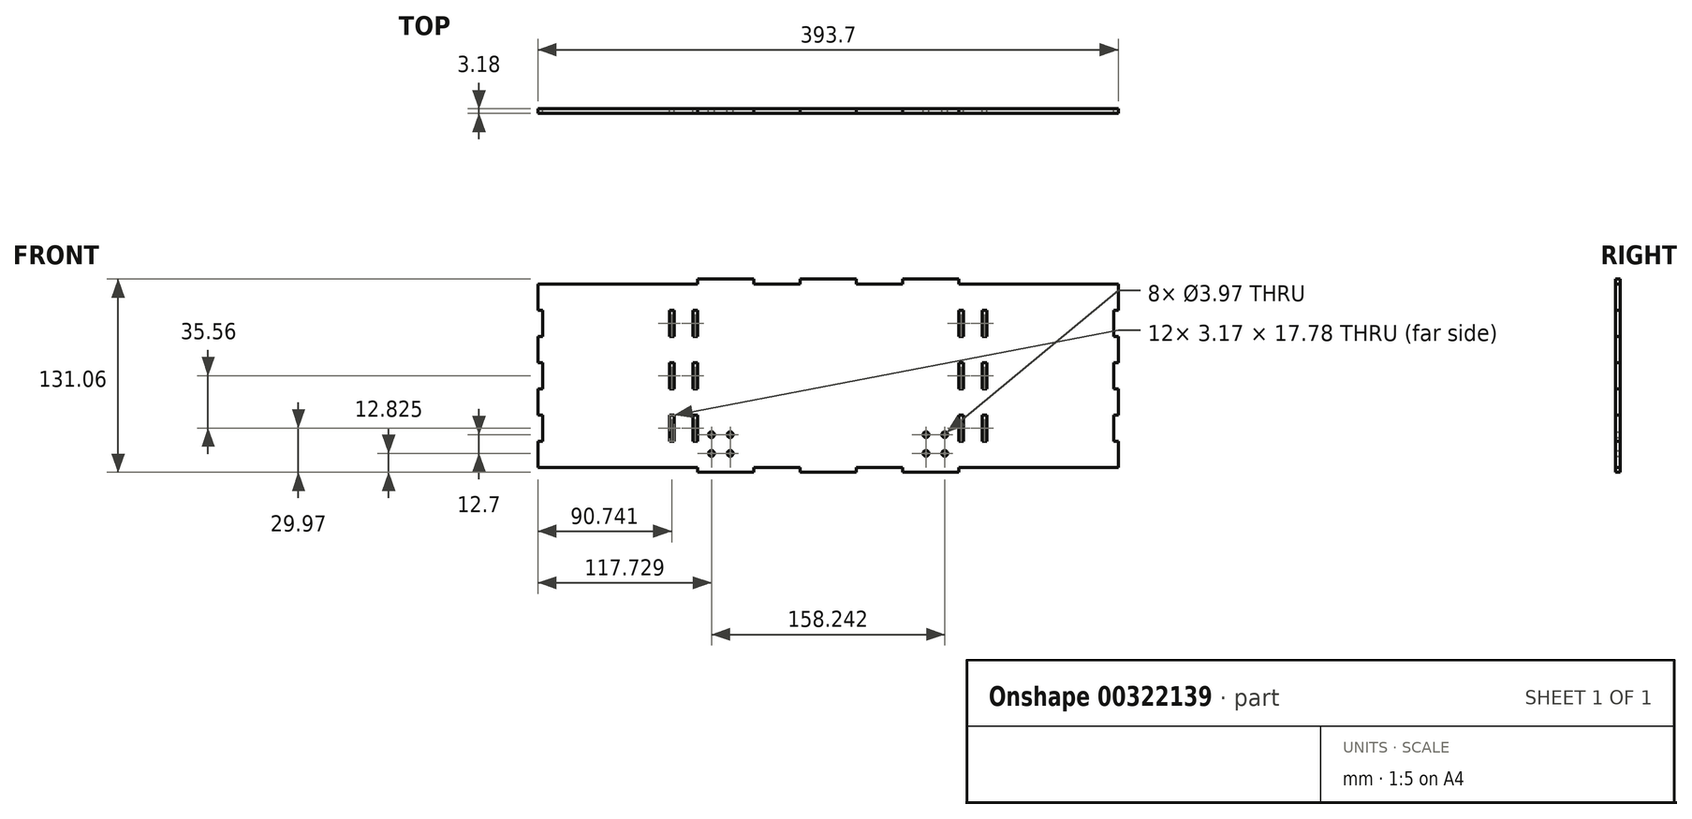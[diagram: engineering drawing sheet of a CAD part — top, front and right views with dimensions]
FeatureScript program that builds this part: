
annotation { "Feature Type Name" : "Feature", "Feature Type Description" : "" }
export const myFeature = defineFeature(function(context is Context, id is Id, definition is map)
    precondition{}
    {
        {
            var Q0;
            Q0=qCreatedBy(makeId("Front.planeOp"),FACE);
            var sketch = newSketch(context, id + "F0", { "sketchPlane" : qUnion([Q0])});
            skLineSegment(sketch, "E0.MirrorCS", {"start": v(-50.55, -65.53) * mm, "end": v(-50.55, -62.23) * mm});
            skLineSegment(sketch, "E1.MirrorCS", {"start": v(19.05, -65.53) * mm, "end": v(19.05, -62.23) * mm});
            skLineSegment(sketch, "E2.MirrorCS", {"start": v(50.55, -65.53) * mm, "end": v(50.55, -62.23) * mm});
            skLineSegment(sketch, "E3.MirrorCS", {"start": v(88.65, -65.53) * mm, "end": v(88.65, -62.23) * mm});
            skLineSegment(sketch, "E4.MirrorCS", {"start": v(-19.05, -65.53) * mm, "end": v(-19.05, -62.23) * mm});
            skLineSegment(sketch, "E5.MirrorCS", {"start": v(88.65, -65.53) * mm, "end": v(50.55, -65.53) * mm});
            skLineSegment(sketch, "E6.MirrorCS", {"start": v(-19.05, -65.53) * mm, "end": v(19.05, -65.53) * mm});
            skLineSegment(sketch, "E7.MirrorCS", {"start": v(-50.55, -65.53) * mm, "end": v(-19.05, -65.53) * mm, "construction": true});
            skLineSegment(sketch, "E8.MirrorCS", {"start": v(-88.65, -65.53) * mm, "end": v(-50.55, -65.53) * mm});
            skLineSegment(sketch, "E9.MirrorCS", {"start": v(-88.65, -65.53) * mm, "end": v(-88.65, -62.23) * mm});
            skLineSegment(sketch, "E10", {"start": v(-107.7, -62.23) * mm, "end": v(-88.65, -62.23) * mm});
            skLineSegment(sketch, "E11.trimOffspring", {"start": v(19.05, -62.23) * mm, "end": v(50.55, -62.23) * mm});
            skLineSegment(sketch, "E12.trimOffspring", {"start": v(-50.55, -62.23) * mm, "end": v(-19.05, -62.23) * mm});
            skLineSegment(sketch, "E13", {"start": v(-107.7, 62.23) * mm, "end": v(-107.7, 44.45) * mm, "construction": true});
            skLineSegment(sketch, "E14.MirrorCS", {"start": v(-104.52, 26.67) * mm, "end": v(-104.52, 8.89) * mm, "construction": true});
            skLineSegment(sketch, "E15.MirrorCS", {"start": v(-107.7, -26.67) * mm, "end": v(-107.7, -8.9) * mm, "construction": true});
            skLineSegment(sketch, "E16.MirrorCS", {"start": v(-104.52, 44.45) * mm, "end": v(-104.52, 26.67) * mm});
            skLineSegment(sketch, "E17.MirrorCS", {"start": v(-104.52, -8.9) * mm, "end": v(-104.52, -26.67) * mm, "construction": true});
            skLineSegment(sketch, "E18.MirrorCS", {"start": v(-104.52, 26.67) * mm, "end": v(-107.7, 26.67) * mm});
            skLineSegment(sketch, "E19.MirrorCS", {"start": v(-107.7, 8.89) * mm, "end": v(-104.52, 8.89) * mm});
            skLineSegment(sketch, "E20.MirrorCS", {"start": v(-104.52, 8.89) * mm, "end": v(-104.52, -8.9) * mm});
            skLineSegment(sketch, "E21.MirrorCS", {"start": v(-104.52, -8.9) * mm, "end": v(-107.7, -8.9) * mm});
            skLineSegment(sketch, "E22.MirrorCS", {"start": v(-107.7, -26.67) * mm, "end": v(-104.52, -26.67) * mm});
            skLineSegment(sketch, "E23.MirrorCS", {"start": v(-107.7, 8.89) * mm, "end": v(-107.7, 26.67) * mm, "construction": true});
            skLineSegment(sketch, "E24.MirrorCS", {"start": v(-104.52, -26.67) * mm, "end": v(-104.52, -44.45) * mm});
            skLineSegment(sketch, "E25.MirrorCS", {"start": v(-104.52, -44.45) * mm, "end": v(-107.7, -44.45) * mm});
            skLineSegment(sketch, "E26.MirrorCS", {"start": v(-107.7, 44.45) * mm, "end": v(-104.52, 44.45) * mm});
            skLineSegment(sketch, "E27.trimOffspring", {"start": v(-107.7, 26.67) * mm, "end": v(-107.7, 8.89) * mm});
            skPoint(sketch, "E28.orphan", {"position": v(-107.7, 8.96) * mm});
            skLineSegment(sketch, "E29.trimOffspring", {"start": v(-107.7, -8.9) * mm, "end": v(-107.7, -26.67) * mm});
            skLineSegment(sketch, "E30.trimOffspring", {"start": v(-107.7, -44.45) * mm, "end": v(-107.7, -62.23) * mm, "construction": true});
            skPoint(sketch, "E31", {"position": v(-104.52, 0) * mm});
            skLineSegment(sketch, "E32.MirrorCS", {"start": v(-50.55, 65.53) * mm, "end": v(-19.05, 65.53) * mm, "construction": true});
            skLineSegment(sketch, "E33.MirrorCS", {"start": v(-88.65, 65.53) * mm, "end": v(-88.65, 62.23) * mm});
            skLineSegment(sketch, "E34.MirrorCS", {"start": v(19.05, 65.53) * mm, "end": v(19.05, 62.23) * mm});
            skLineSegment(sketch, "E35.MirrorCS", {"start": v(88.65, 65.53) * mm, "end": v(88.65, 62.23) * mm});
            skLineSegment(sketch, "E36.MirrorCS", {"start": v(88.65, 65.53) * mm, "end": v(50.55, 65.53) * mm});
            skLineSegment(sketch, "E37.MirrorCS", {"start": v(-88.65, 65.53) * mm, "end": v(-50.55, 65.53) * mm});
            skLineSegment(sketch, "E38.MirrorCS", {"start": v(-107.7, 62.23) * mm, "end": v(-88.65, 62.23) * mm});
            skLineSegment(sketch, "E39.MirrorCS", {"start": v(19.05, 62.23) * mm, "end": v(50.55, 62.23) * mm});
            skLineSegment(sketch, "E40.MirrorCS", {"start": v(-50.55, 62.23) * mm, "end": v(-19.05, 62.23) * mm});
            skLineSegment(sketch, "E41.MirrorCS", {"start": v(-50.55, 65.53) * mm, "end": v(-50.55, 62.23) * mm});
            skLineSegment(sketch, "E42.MirrorCS", {"start": v(50.55, 65.53) * mm, "end": v(50.55, 62.23) * mm});
            skLineSegment(sketch, "E43.MirrorCS", {"start": v(-19.05, 65.53) * mm, "end": v(-19.05, 62.23) * mm});
            skLineSegment(sketch, "E44.MirrorCS", {"start": v(-19.05, 65.53) * mm, "end": v(19.05, 65.53) * mm});
            skPoint(sketch, "E45", {"position": v(0, 65.53) * mm});
            skPoint(sketch, "E46.oppositeSnap0", {"position": v(-106.1, 26.67) * mm});
            skLineSegment(sketch, "E46.bottom", {"start": v(-91.82, 44.45) * mm, "end": v(-88.65, 44.45) * mm});
            skLineSegment(sketch, "E46.top", {"start": v(-91.82, 26.67) * mm, "end": v(-88.65, 26.67) * mm});
            skLineSegment(sketch, "E46.left", {"start": v(-91.82, 44.45) * mm, "end": v(-91.82, 26.67) * mm});
            skLineSegment(sketch, "E46.right", {"start": v(-88.65, 44.45) * mm, "end": v(-88.65, 26.67) * mm});
            skLineSegment(sketch, "E47.bottom", {"start": v(-91.82, 8.89) * mm, "end": v(-88.65, 8.89) * mm});
            skLineSegment(sketch, "E47.top", {"start": v(-91.82, -8.89) * mm, "end": v(-88.65, -8.89) * mm});
            skLineSegment(sketch, "E47.left", {"start": v(-91.82, 8.9) * mm, "end": v(-91.82, -8.9) * mm});
            skLineSegment(sketch, "E47.right", {"start": v(-88.65, 8.9) * mm, "end": v(-88.65, -8.9) * mm});
            skLineSegment(sketch, "E48.bottom", {"start": v(-88.65, -44.45) * mm, "end": v(-91.82, -44.45) * mm});
            skLineSegment(sketch, "E48.top", {"start": v(-88.65, -26.67) * mm, "end": v(-91.82, -26.67) * mm});
            skLineSegment(sketch, "E48.left", {"start": v(-88.65, -44.45) * mm, "end": v(-88.65, -26.67) * mm});
            skLineSegment(sketch, "E48.right", {"start": v(-91.82, -44.45) * mm, "end": v(-91.82, -26.67) * mm});
            skLineSegment(sketch, "E49.MirrorCS", {"start": v(91.82, 8.89) * mm, "end": v(88.65, 8.89) * mm});
            skLineSegment(sketch, "E50.MirrorCS", {"start": v(88.65, -26.67) * mm, "end": v(91.82, -26.67) * mm});
            skLineSegment(sketch, "E51.MirrorCS", {"start": v(91.82, 26.67) * mm, "end": v(88.65, 26.67) * mm});
            skLineSegment(sketch, "E52.MirrorCS", {"start": v(88.65, -44.45) * mm, "end": v(91.82, -44.45) * mm});
            skLineSegment(sketch, "E53.MirrorCS", {"start": v(91.82, 44.45) * mm, "end": v(88.65, 44.45) * mm});
            skLineSegment(sketch, "E54.MirrorCS", {"start": v(91.82, -8.89) * mm, "end": v(88.65, -8.89) * mm});
            skLineSegment(sketch, "E55.MirrorCS", {"start": v(91.82, -44.45) * mm, "end": v(91.82, -26.67) * mm});
            skLineSegment(sketch, "E56.MirrorCS", {"start": v(88.65, 44.45) * mm, "end": v(88.65, 26.67) * mm});
            skLineSegment(sketch, "E57.MirrorCS", {"start": v(88.65, -44.45) * mm, "end": v(88.65, -26.67) * mm});
            skLineSegment(sketch, "E58.MirrorCS", {"start": v(91.82, 44.45) * mm, "end": v(91.82, 26.67) * mm});
            skLineSegment(sketch, "E59.MirrorCS", {"start": v(88.65, 8.9) * mm, "end": v(88.65, -8.9) * mm});
            skLineSegment(sketch, "E60.MirrorCS", {"start": v(91.82, 8.9) * mm, "end": v(91.82, -8.9) * mm});
            skLineSegment(sketch, "E61", {"start": v(-104.52, -44.45) * mm, "end": v(-104.52, -62.23) * mm, "construction": true});
            skCircle(sketch, "E62", {"center": v(-79.12, -52.7) * mm, "radius": 1.98 * mm});
            skCircle(sketch, "E63", {"center": v(-79.12, -40) * mm, "radius": 1.98 * mm});
            skCircle(sketch, "E64", {"center": v(-66.42, -52.7) * mm, "radius": 1.98 * mm});
            skCircle(sketch, "E65", {"center": v(-66.42, -40) * mm, "radius": 1.98 * mm});
            skCircle(sketch, "E66.MirrorC", {"center": v(79.12, -52.7) * mm, "radius": 1.98 * mm});
            skCircle(sketch, "E67.MirrorC", {"center": v(79.12, -40) * mm, "radius": 1.98 * mm});
            skCircle(sketch, "E68.MirrorC", {"center": v(66.42, -52.7) * mm, "radius": 1.98 * mm});
            skCircle(sketch, "E69.MirrorC", {"center": v(66.42, -40) * mm, "radius": 1.98 * mm});
            skPoint(sketch, "E70.1.0.0", {"position": v(-195.26, 26.67) * mm});
            skLineSegment(sketch, "E70.1.0.1", {"start": v(-193.68, 8.89) * mm, "end": v(-193.68, -8.9) * mm});
            skLineSegment(sketch, "E70.1.0.2", {"start": v(-193.68, -44.45) * mm, "end": v(-193.68, -62.23) * mm, "construction": true});
            skLineSegment(sketch, "E70.1.0.3", {"start": v(-193.68, -26.67) * mm, "end": v(-193.68, -44.45) * mm});
            skPoint(sketch, "E70.1.0.4", {"position": v(-196.85, 8.96) * mm});
            skLineSegment(sketch, "E70.1.0.5", {"start": v(-196.85, 26.67) * mm, "end": v(-196.85, 8.89) * mm});
            skLineSegment(sketch, "E70.1.0.6", {"start": v(-196.85, -44.45) * mm, "end": v(-196.85, -62.23) * mm});
            skPoint(sketch, "E70.1.0.7", {"position": v(-193.68, 0) * mm});
            skLineSegment(sketch, "E70.1.0.8", {"start": v(-196.85, 62.23) * mm, "end": v(-196.85, 44.45) * mm});
            skLineSegment(sketch, "E70.1.0.9", {"start": v(-193.68, 26.67) * mm, "end": v(-193.68, 8.89) * mm, "construction": true});
            skLineSegment(sketch, "E70.1.0.10", {"start": v(-196.85, -26.67) * mm, "end": v(-196.85, -8.89) * mm});
            skLineSegment(sketch, "E70.1.0.11", {"start": v(-193.68, 44.45) * mm, "end": v(-193.68, 26.67) * mm});
            skLineSegment(sketch, "E70.1.0.12", {"start": v(-193.68, -8.9) * mm, "end": v(-193.68, -26.67) * mm, "construction": true});
            skLineSegment(sketch, "E70.1.0.13", {"start": v(-196.85, 8.89) * mm, "end": v(-196.85, 26.67) * mm});
            skLineSegment(sketch, "E70.1.0.14", {"start": v(-196.85, -8.89) * mm, "end": v(-196.85, -26.67) * mm});
            skLineSegment(sketch, "E70.1.0.15", {"start": v(-193.68, -44.45) * mm, "end": v(-196.85, -44.45) * mm});
            skLineSegment(sketch, "E70.1.0.16", {"start": v(-196.85, 44.45) * mm, "end": v(-193.68, 44.45) * mm});
            skLineSegment(sketch, "E70.1.0.17", {"start": v(-193.68, -8.89) * mm, "end": v(-196.85, -8.89) * mm});
            skLineSegment(sketch, "E70.1.0.18", {"start": v(-196.85, -26.67) * mm, "end": v(-193.68, -26.67) * mm});
            skLineSegment(sketch, "E70.1.0.19", {"start": v(-193.68, 26.67) * mm, "end": v(-196.85, 26.67) * mm});
            skLineSegment(sketch, "E70.1.0.20", {"start": v(-196.85, 8.89) * mm, "end": v(-193.68, 8.89) * mm});
            skLineSegment(sketch, "E70.direction1", {"start": v(-107.7, -62.23) * mm, "end": v(-196.85, -62.23) * mm, "construction": true});
            skLineSegment(sketch, "E71", {"start": v(-107.7, 62.23) * mm, "end": v(-196.85, 62.23) * mm});
            skLineSegment(sketch, "E72", {"start": v(-107.7, -62.23) * mm, "end": v(-196.85, -62.23) * mm});
            skLineSegment(sketch, "E73", {"start": v(-107.7, 44.45) * mm, "end": v(-107.7, -44.45) * mm});
            skLineSegment(sketch, "E74.MirrorCS", {"start": v(107.7, -62.23) * mm, "end": v(88.65, -62.23) * mm});
            skLineSegment(sketch, "E75.MirrorCS", {"start": v(107.7, 62.23) * mm, "end": v(88.65, 62.23) * mm});
            skLineSegment(sketch, "E76.MirrorCS", {"start": v(104.52, 26.67) * mm, "end": v(107.7, 26.67) * mm});
            skLineSegment(sketch, "E77.MirrorCS", {"start": v(107.7, 8.89) * mm, "end": v(104.52, 8.89) * mm});
            skLineSegment(sketch, "E78.MirrorCS", {"start": v(193.68, 26.67) * mm, "end": v(196.85, 26.67) * mm});
            skLineSegment(sketch, "E79.MirrorCS", {"start": v(196.85, 8.89) * mm, "end": v(193.68, 8.89) * mm});
            skLineSegment(sketch, "E80.MirrorCS", {"start": v(196.85, -26.67) * mm, "end": v(193.68, -26.67) * mm});
            skLineSegment(sketch, "E81.MirrorCS", {"start": v(193.68, -44.45) * mm, "end": v(196.85, -44.45) * mm});
            skLineSegment(sketch, "E82.MirrorCS", {"start": v(104.52, -44.45) * mm, "end": v(107.7, -44.45) * mm});
            skLineSegment(sketch, "E83.MirrorCS", {"start": v(107.7, -26.67) * mm, "end": v(104.52, -26.67) * mm});
            skLineSegment(sketch, "E84.MirrorCS", {"start": v(193.68, -8.89) * mm, "end": v(196.85, -8.89) * mm});
            skLineSegment(sketch, "E85.MirrorCS", {"start": v(107.7, 44.45) * mm, "end": v(104.52, 44.45) * mm});
            skLineSegment(sketch, "E86.MirrorCS", {"start": v(104.52, -8.89) * mm, "end": v(107.7, -8.89) * mm});
            skLineSegment(sketch, "E87.MirrorCS", {"start": v(196.85, 44.45) * mm, "end": v(193.68, 44.45) * mm});
            skLineSegment(sketch, "E88.MirrorCS", {"start": v(107.7, -62.23) * mm, "end": v(196.85, -62.23) * mm});
            skLineSegment(sketch, "E89.MirrorCS", {"start": v(107.7, 26.67) * mm, "end": v(107.7, 8.89) * mm});
            skLineSegment(sketch, "E90.MirrorCS", {"start": v(196.85, -26.67) * mm, "end": v(196.85, -8.89) * mm});
            skLineSegment(sketch, "E91.MirrorCS", {"start": v(196.85, 8.89) * mm, "end": v(196.85, 26.67) * mm});
            skLineSegment(sketch, "E92.MirrorCS", {"start": v(193.68, 8.89) * mm, "end": v(193.68, -8.9) * mm});
            skLineSegment(sketch, "E93.MirrorCS", {"start": v(107.7, -8.89) * mm, "end": v(107.7, -26.67) * mm});
            skLineSegment(sketch, "E94.MirrorCS", {"start": v(104.52, 8.9) * mm, "end": v(104.52, -8.9) * mm});
            skPoint(sketch, "E95.MirrorP", {"position": v(107.7, 8.96) * mm});
            skPoint(sketch, "E96.MirrorP", {"position": v(193.68, 0) * mm});
            skLineSegment(sketch, "E97.MirrorCS", {"start": v(107.7, 44.45) * mm, "end": v(107.7, -44.45) * mm});
            skLineSegment(sketch, "E98.MirrorCS", {"start": v(196.85, 62.23) * mm, "end": v(196.85, 44.45) * mm});
            skLineSegment(sketch, "E99.MirrorCS", {"start": v(104.52, -8.9) * mm, "end": v(104.52, -26.67) * mm, "construction": true});
            skPoint(sketch, "E100.MirrorP", {"position": v(196.85, 8.96) * mm});
            skLineSegment(sketch, "E101.MirrorCS", {"start": v(104.52, -26.67) * mm, "end": v(104.52, -44.45) * mm});
            skPoint(sketch, "E102.MirrorP", {"position": v(195.26, 26.67) * mm});
            skLineSegment(sketch, "E103.MirrorCS", {"start": v(196.85, -8.89) * mm, "end": v(196.85, -26.67) * mm});
            skLineSegment(sketch, "E104.MirrorCS", {"start": v(107.7, 8.89) * mm, "end": v(107.7, 26.67) * mm, "construction": true});
            skLineSegment(sketch, "E105.MirrorCS", {"start": v(107.7, -26.67) * mm, "end": v(107.7, -8.89) * mm, "construction": true});
            skLineSegment(sketch, "E106.MirrorCS", {"start": v(104.52, 26.67) * mm, "end": v(104.52, 8.9) * mm, "construction": true});
            skLineSegment(sketch, "E107.MirrorCS", {"start": v(107.7, 62.23) * mm, "end": v(107.7, 44.45) * mm, "construction": true});
            skLineSegment(sketch, "E108.MirrorCS", {"start": v(107.7, 62.23) * mm, "end": v(196.85, 62.23) * mm});
            skLineSegment(sketch, "E109.MirrorCS", {"start": v(193.68, 26.67) * mm, "end": v(193.68, 8.89) * mm, "construction": true});
            skLineSegment(sketch, "E110.MirrorCS", {"start": v(196.85, -44.45) * mm, "end": v(196.85, -62.23) * mm});
            skLineSegment(sketch, "E111.MirrorCS", {"start": v(104.52, 44.45) * mm, "end": v(104.52, 26.67) * mm});
            skPoint(sketch, "E112.MirrorP", {"position": v(106.1, 26.67) * mm});
            skLineSegment(sketch, "E113.MirrorCS", {"start": v(104.52, -44.45) * mm, "end": v(104.52, -62.23) * mm, "construction": true});
            skLineSegment(sketch, "E114.MirrorCS", {"start": v(196.85, 26.67) * mm, "end": v(196.85, 8.89) * mm});
            skLineSegment(sketch, "E115.MirrorCS", {"start": v(107.7, -62.23) * mm, "end": v(196.85, -62.23) * mm, "construction": true});
            skPoint(sketch, "E116.MirrorP", {"position": v(104.52, 0) * mm});
            skLineSegment(sketch, "E117.MirrorCS", {"start": v(193.68, -8.9) * mm, "end": v(193.68, -26.67) * mm, "construction": true});
            skLineSegment(sketch, "E118.MirrorCS", {"start": v(193.68, -26.67) * mm, "end": v(193.68, -44.45) * mm});
            skLineSegment(sketch, "E119.MirrorCS", {"start": v(193.68, -44.45) * mm, "end": v(193.68, -62.23) * mm, "construction": true});
            skLineSegment(sketch, "E120.MirrorCS", {"start": v(107.7, -44.45) * mm, "end": v(107.7, -62.23) * mm, "construction": true});
            skLineSegment(sketch, "E121.MirrorCS", {"start": v(193.68, 44.45) * mm, "end": v(193.68, 26.67) * mm});
            skSolve(sketch);
        }
        {
            var Q0;
            Q0=makeQuery(id+"F0.imprint","IMPRINT",FACE,{"disambiguationData":[TD([[makeQuery(id+"F0.imprint","IMPRINT",EDGE,{"derivedFrom":sQuery(id+"F0.wireOp",EDGE,"E0.MirrorCS")}),1.0]])]});
            extrude(context, id + "F1", {"entities" : qUnion([Q0]), "depth" : 3.17 * mm});
        }
    });
